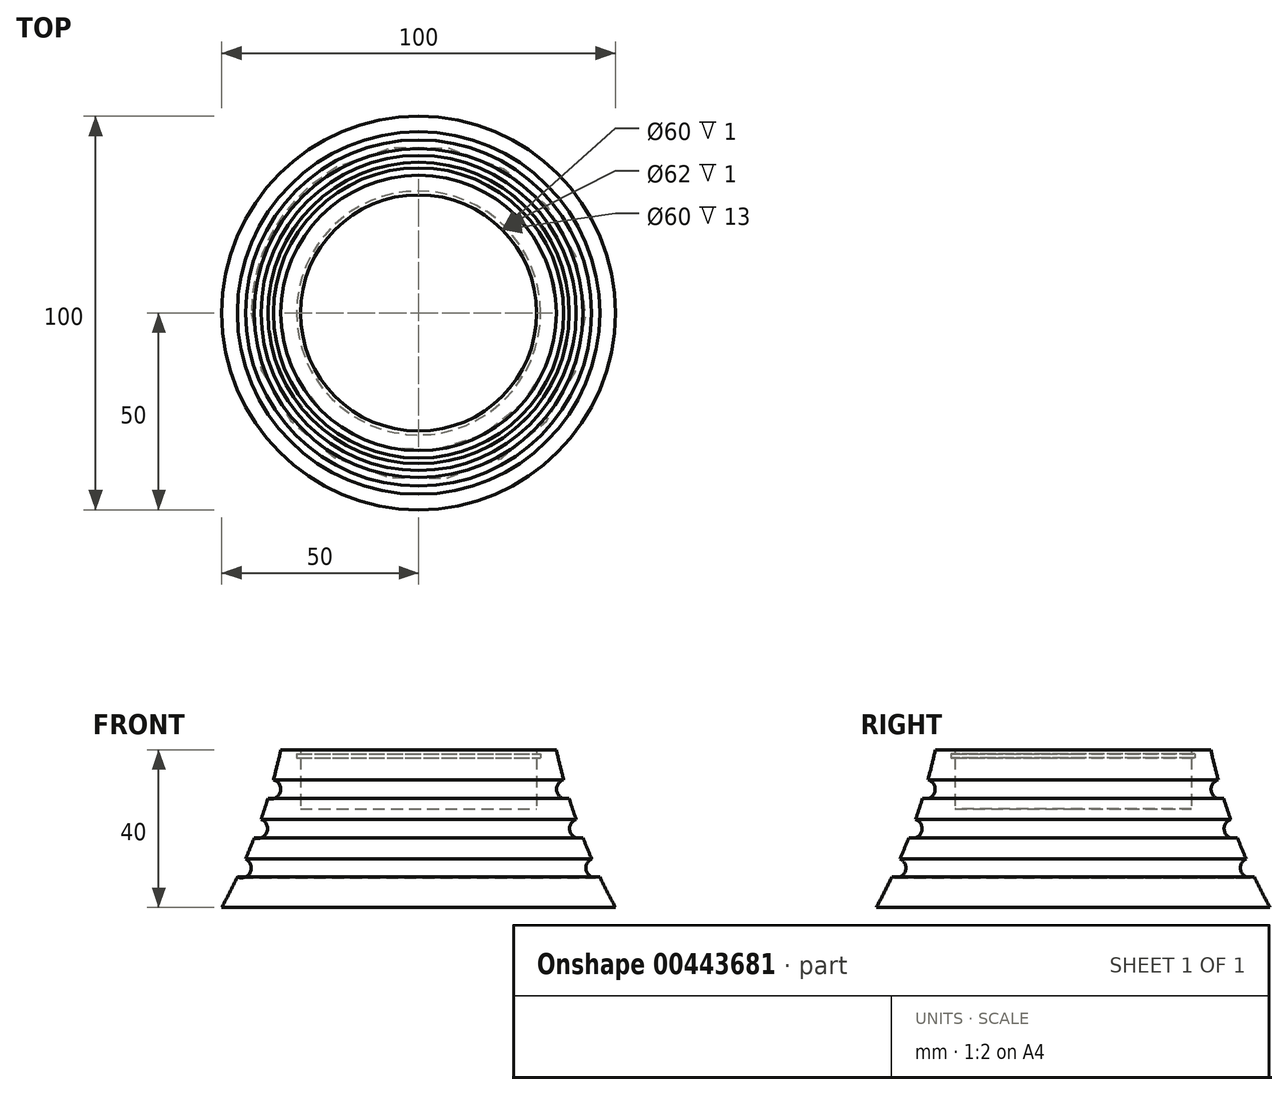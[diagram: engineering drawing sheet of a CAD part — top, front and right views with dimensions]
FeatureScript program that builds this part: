
annotation { "Feature Type Name" : "Feature", "Feature Type Description" : "" }
export const myFeature = defineFeature(function(context is Context, id is Id, definition is map)
    precondition{}
    {
        {
            var Q0;
            Q0=qCreatedBy(makeId("Front.planeOp"),FACE);
            var sketch = newSketch(context, id + "F0", { "sketchPlane" : qUnion([Q0])});
            skLineSegment(sketch, "E0", {"start": v(0, 0) * mm, "end": v(-50, 0) * mm});
            skLineSegment(sketch, "E1", {"start": v(-50, 0) * mm, "end": v(-50, 25) * mm});
            skLineSegment(sketch, "E2", {"start": v(-50, 25) * mm, "end": v(-20, 25) * mm});
            skLineSegment(sketch, "E3", {"start": v(-20, 25) * mm, "end": v(-20, 38) * mm});
            skLineSegment(sketch, "E4", {"start": v(-20, 40) * mm, "end": v(-15, 40) * mm});
            skArc(sketch, "E5", {"start": v(-15, 40) * mm, "mid": v(-14.11, 36.2) * mm, "end": v(-13.13, 32.4) * mm});
            skLineSegment(sketch, "E6.bottom", {"start": v(-20, 39) * mm, "end": v(-19, 39) * mm});
            skLineSegment(sketch, "E6.top", {"start": v(-20, 38) * mm, "end": v(-19, 38) * mm});
            skLineSegment(sketch, "E6.right", {"start": v(-19, 39) * mm, "end": v(-19, 38) * mm});
            skLineSegment(sketch, "E7.trimOffspring", {"start": v(-20, 39) * mm, "end": v(-20, 40) * mm});
            skArc(sketch, "E8", {"start": v(-13.13, 32.4) * mm, "mid": v(-14.84, 29.3) * mm, "end": v(-11.72, 27.6) * mm});
            skArc(sketch, "E9", {"start": v(-9.98, 22.35) * mm, "mid": v(-11.48, 19.13) * mm, "end": v(-8.24, 17.66) * mm});
            skArc(sketch, "E10", {"start": v(-6.03, 12.28) * mm, "mid": v(-7.28, 8.96) * mm, "end": v(-3.95, 7.73) * mm});
            skArc(sketch, "E11.trimOffspring", {"start": v(-3.95, 7.73) * mm, "mid": v(-2.03, 3.84) * mm, "end": v(0, 0) * mm});
            skArc(sketch, "E12.trimOffspring", {"start": v(-8.24, 17.66) * mm, "mid": v(-7.16, 14.96) * mm, "end": v(-6.03, 12.28) * mm});
            skArc(sketch, "E13.trimOffspring", {"start": v(-11.72, 27.6) * mm, "mid": v(-10.88, 24.97) * mm, "end": v(-9.98, 22.35) * mm});
            skSolve(sketch);
        }
        {
            var Q0;
            Q0=makeQuery(id+"F0.imprint","IMPRINT",FACE,{"disambiguationData":[TD([[makeQuery(id+"F0.imprint","IMPRINT",EDGE,{"derivedFrom":sQuery(id+"F0.wireOp",EDGE,"E0")}),-1.0]])]});
            var Q1;
            Q1=sQuery(id+"F0.wireOp",EDGE,"E1");
            revolve(context, id + "F1", {"entities" : qUnion([Q0]), "axis" : qUnion([Q1]), "revolveType" : RevolveType.FULL});
        }
    });
